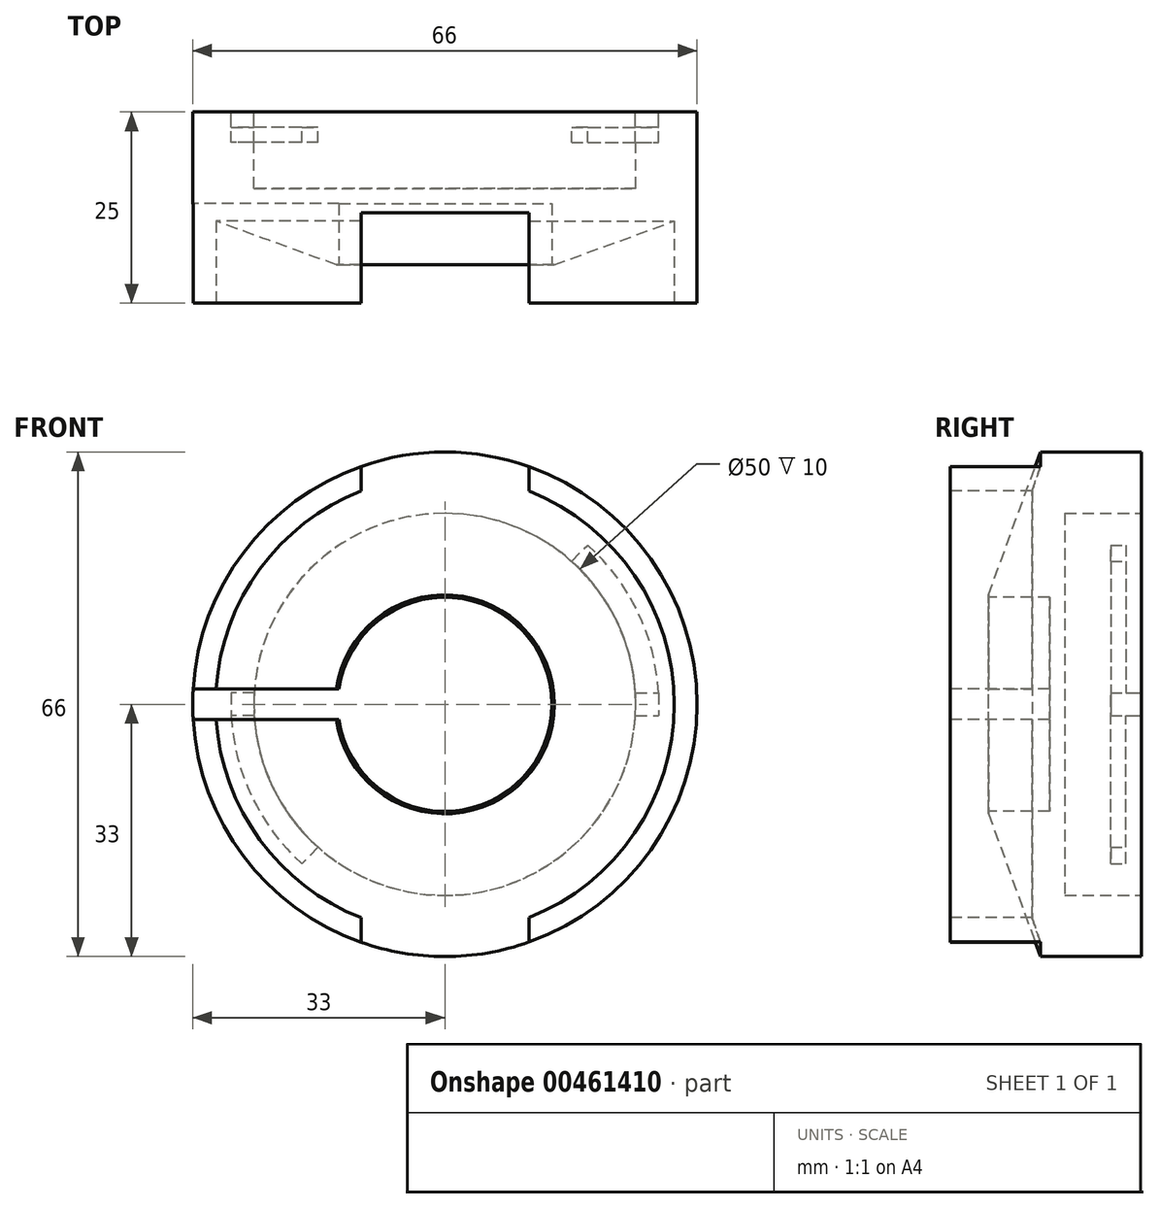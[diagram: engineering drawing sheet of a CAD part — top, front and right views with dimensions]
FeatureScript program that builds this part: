
annotation { "Feature Type Name" : "Feature", "Feature Type Description" : "" }
export const myFeature = defineFeature(function(context is Context, id is Id, definition is map)
    precondition{}
    {
        {
            var Q0;
            Q0=qCreatedBy(makeId("Front.planeOp"),FACE);
            var sketch = newSketch(context, id + "F0", { "sketchPlane" : qUnion([Q0])});
            skCircle(sketch, "E0", {"center": v(0, 0) * mm, "radius": 30 * mm});
            skSolve(sketch);
        }
        {
            var Q0;
            Q0 = qSketchRegion(id + "F0", true);
            extrude(context, id + "F1", {"entities" : qUnion([Q0]), "depth" : 20 * mm});
        }
        {
            var Q0;
            Q0=makeQuery(id+"F1.opExtrude","CAP_FACE",FACE,{"disambiguationData":[OSD([sQuery(id+"F0.wireOp",EDGE,"E0")])],"isStart":false});
            var sketch = newSketch(context, id + "F2", { "sketchPlane" : qUnion([Q0])});
            skCircle(sketch, "E1", {"center": v(0, 0) * mm, "radius": 33 * mm});
            skCircle(sketch, "E2", {"center": v(0, 0) * mm, "radius": 30 * mm});
            skSolve(sketch);
        }
        {
            var Q0;
            Q0=makeQuery(id+"F2.imprint","IMPRINT",FACE,{"disambiguationData":[TD([[makeQuery(id+"F2.imprint","IMPRINT",EDGE,{"derivedFrom":sQuery(id+"F2.wireOp",EDGE,"E1")}),1.0]])]});
            var Q1;
            Q1=makeQuery(id+"F1.opExtrude","CAP_FACE",FACE,{"disambiguationData":[OSD([sQuery(id+"F0.wireOp",EDGE,"E0")])],"isStart":true});
            extrude(context, id + "F3", {"entities" : qUnion([Q0]), "operationType" : NewBodyOperationType.ADD, "endBound" : BoundingType.UP_TO_SURFACE, "oppositeDirection" : true, "endBoundEntityFace" : qUnion([Q1]), "depth" : 25 * mm, "hasSecondDirection" : true, "secondDirectionOppositeDirection" : false, "secondDirectionDepth" : 5 * mm});
        }
        {
            var Q0;
            Q0=makeQuery(id+"F1.opExtrude","CAP_FACE",FACE,{"disambiguationData":[OSD([sQuery(id+"F0.wireOp",EDGE,"E0")])],"isStart":false});
            var sketch = newSketch(context, id + "F4", { "sketchPlane" : qUnion([Q0])});
            skCircle(sketch, "E3", {"center": v(0, 0) * mm, "radius": 14 * mm});
            skSolve(sketch);
        }
        {
            var Q0;
            Q0 = qSketchRegion(id + "F4", true);
            extrude(context, id + "F5", {"entities" : qUnion([Q0]), "operationType" : NewBodyOperationType.REMOVE, "oppositeDirection" : true, "depth" : 8 * mm});
        }
        {
            var Q0;
            Q0=makeQuery(id+"F3.opExtrude","CAP_FACE",FACE,{"disambiguationData":[OSD([sQuery(id+"F2.wireOp",EDGE,"E1"),sQuery(id+"F2.wireOp",EDGE,"E2")])],"isStart":true});
            var sketch = newSketch(context, id + "F6", { "sketchPlane" : qUnion([Q0])});
            skLineSegment(sketch, "E4.bottom", {"start": v(-33, 2) * mm, "end": v(0, 2) * mm});
            skLineSegment(sketch, "E4.top", {"start": v(-33, -2) * mm, "end": v(0, -2) * mm});
            skLineSegment(sketch, "E4.left", {"start": v(-33, 2) * mm, "end": v(-33, -2) * mm});
            skLineSegment(sketch, "E4.right", {"start": v(0, 2) * mm, "end": v(0, -2) * mm});
            skSolve(sketch);
        }
        {
            var Q0;
            Q0 = qSketchRegion(id + "F6", true);
            var Q1;
            Q1=makeQuery(id+"F5.boolean.opBoolean","COPY",FACE,{"derivedFrom":makeQuery(id+"F5.opExtrude","CAP_FACE",FACE,{"disambiguationData":[OSD([sQuery(id+"F4.wireOp",EDGE,"E3")])],"isStart":false})});
            extrude(context, id + "F7", {"entities" : qUnion([Q0]), "operationType" : NewBodyOperationType.REMOVE, "endBound" : BoundingType.UP_TO_SURFACE, "oppositeDirection" : true, "endBoundEntityFace" : qUnion([Q1]), "depth" : 25 * mm});
        }
        {
            var Q0;
            Q0=makeQuery(id+"F3.opExtrude","CAP_FACE",FACE,{"disambiguationData":[OSD([sQuery(id+"F2.wireOp",EDGE,"E1"),sQuery(id+"F2.wireOp",EDGE,"E2")])],"isStart":true});
            var sketch = newSketch(context, id + "F8", { "sketchPlane" : qUnion([Q0])});
            skLineSegment(sketch, "E5.bottom", {"start": v(-10.97, 33) * mm, "end": v(11.03, 33) * mm});
            skLineSegment(sketch, "E5.top", {"start": v(-10.97, -33) * mm, "end": v(11.03, -33) * mm});
            skLineSegment(sketch, "E5.left", {"start": v(-10.97, 33) * mm, "end": v(-10.97, -33) * mm});
            skLineSegment(sketch, "E5.right", {"start": v(11.03, 33) * mm, "end": v(11.03, -33) * mm});
            skLineSegment(sketch, "E6", {"start": v(33, 0) * mm, "end": v(33, 26.84) * mm, "construction": true});
            skLineSegment(sketch, "E7", {"start": v(33, 26.84) * mm, "end": v(33, -25.37) * mm, "construction": true});
            skLineSegment(sketch, "E8.MirrorCS", {"start": v(-33, 26.84) * mm, "end": v(-33, -25.37) * mm, "construction": true});
            skLineSegment(sketch, "E9", {"start": v(33, 0) * mm, "end": v(11.03, 0) * mm, "construction": true});
            skLineSegment(sketch, "E10", {"start": v(-10.97, 0) * mm, "end": v(-32.94, 0) * mm, "construction": true});
            skSolve(sketch);
        }
        {
            var Q0;
            Q0 = qSketchRegion(id + "F8", true);
            var Q1;
            Q1=makeQuery(id+"F1.opExtrude","CAP_FACE",FACE,{"disambiguationData":[OSD([sQuery(id+"F0.wireOp",EDGE,"E0")])],"isStart":false});
            extrude(context, id + "F9", {"entities" : qUnion([Q0]), "operationType" : NewBodyOperationType.REMOVE, "endBound" : BoundingType.UP_TO_SURFACE, "oppositeDirection" : true, "endBoundEntityFace" : qUnion([Q1]), "depth" : 25 * mm});
        }
        {
            var Q0;
            Q0=makeQuery(id+"F3.boolean.opBoolean","MERGE",FACE,{"derivedFrom":[makeQuery(id+"F1.opExtrude","CAP_FACE",FACE,{"disambiguationData":[OSD([sQuery(id+"F0.wireOp",EDGE,"E0")])],"isStart":true}),makeQuery(id+"F3.opExtrude","CAP_FACE",FACE,{"disambiguationData":[OSD([sQuery(id+"F2.wireOp",EDGE,"E1"),sQuery(id+"F2.wireOp",EDGE,"E2")])],"isStart":false})]});
            var sketch = newSketch(context, id + "F10", { "sketchPlane" : qUnion([Q0])});
            skCircle(sketch, "E11", {"center": v(0, 0) * mm, "radius": 25 * mm});
            skSolve(sketch);
        }
        {
            var Q0;
            Q0 = qSketchRegion(id + "F10", true);
            extrude(context, id + "F11", {"entities" : qUnion([Q0]), "operationType" : NewBodyOperationType.REMOVE, "oppositeDirection" : true, "depth" : 10 * mm});
        }
        {
            var Q0;
            Q0=makeQuery(id+"F3.boolean.opBoolean","MERGE",FACE,{"derivedFrom":[makeQuery(id+"F1.opExtrude","CAP_FACE",FACE,{"disambiguationData":[OSD([sQuery(id+"F0.wireOp",EDGE,"E0")])],"isStart":true}),makeQuery(id+"F3.opExtrude","CAP_FACE",FACE,{"disambiguationData":[OSD([sQuery(id+"F2.wireOp",EDGE,"E1"),sQuery(id+"F2.wireOp",EDGE,"E2")])],"isStart":false})]});
            var sketch = newSketch(context, id + "F12", { "sketchPlane" : qUnion([Q0])});
            skLineSegment(sketch, "E12.bottom", {"start": v(-24.95, 1.5) * mm, "end": v(-27.95, 1.5) * mm});
            skLineSegment(sketch, "E12.top", {"start": v(-24.95, -1.5) * mm, "end": v(-27.95, -1.5) * mm});
            skLineSegment(sketch, "E12.left", {"start": v(-24.95, 1.5) * mm, "end": v(-24.95, -1.5) * mm});
            skLineSegment(sketch, "E12.right", {"start": v(-27.95, 1.5) * mm, "end": v(-27.95, -1.5) * mm});
            skPoint(sketch, "E12.middle", {"position": v(-26.45, 0) * mm});
            skLineSegment(sketch, "E13.MirrorCS", {"start": v(24.95, 1.5) * mm, "end": v(27.95, 1.5) * mm});
            skLineSegment(sketch, "E14.MirrorCS", {"start": v(24.95, -1.5) * mm, "end": v(27.95, -1.5) * mm});
            skLineSegment(sketch, "E15.MirrorCS", {"start": v(24.95, 1.5) * mm, "end": v(24.95, -1.5) * mm});
            skLineSegment(sketch, "E16.MirrorCS", {"start": v(27.95, 1.5) * mm, "end": v(27.95, -1.5) * mm});
            skPoint(sketch, "E17.MirrorP", {"position": v(26.45, 0) * mm});
            skSolve(sketch);
        }
        {
            var Q0;
            Q0 = qSketchRegion(id + "F12", true);
            extrude(context, id + "F13", {"entities" : qUnion([Q0]), "operationType" : NewBodyOperationType.REMOVE, "oppositeDirection" : true, "depth" : 4 * mm});
        }
        {
            var Q0;
            Q0=makeQuery(id+"F13.boolean.opBoolean","COPY",FACE,{"derivedFrom":makeQuery(id+"F13.opExtrude","SWEPT_FACE",FACE,{"disambiguationData":[OSD([sQuery(id+"F12.wireOp",EDGE,"E14.MirrorCS")])]})});
            var sketch = newSketch(context, id + "F14", { "sketchPlane" : qUnion([Q0])});
            skLineSegment(sketch, "E18.bottom", {"start": v(-27.95, -4) * mm, "end": v(-24.95, -4) * mm});
            skLineSegment(sketch, "E18.top", {"start": v(-27.95, -2) * mm, "end": v(-24.95, -2) * mm});
            skLineSegment(sketch, "E18.left", {"start": v(-27.95, -4) * mm, "end": v(-27.95, -2) * mm});
            skLineSegment(sketch, "E18.right", {"start": v(-24.95, -4) * mm, "end": v(-24.95, -2) * mm});
            skSolve(sketch);
        }
        {
            var Q0;
            Q0 = qSketchRegion(id + "F14", true);
            var Q1;
            Q1=makeQuery(id+"F11.boolean.opBoolean","COPY",FACE,{"derivedFrom":makeQuery(id+"F11.opExtrude","SWEPT_FACE",FACE,{"disambiguationData":[OSD([sQuery(id+"F10.wireOp",EDGE,"E11")])]})});
            revolve(context, id + "F15", {"operationType" : NewBodyOperationType.REMOVE, "entities" : qUnion([Q0]), "axis" : qUnion([Q1]), "revolveType" : RevolveType.ONE_DIRECTION, "angle" : 45 * degree});
        }
        {
            var Q0;
            Q0=makeQuery(id+"F13.boolean.opBoolean","COPY",FACE,{"derivedFrom":makeQuery(id+"F13.opExtrude","SWEPT_FACE",FACE,{"disambiguationData":[OSD([sQuery(id+"F12.wireOp",EDGE,"E12.bottom")])]})});
            var sketch = newSketch(context, id + "F16", { "sketchPlane" : qUnion([Q0])});
            skLineSegment(sketch, "E19.bottom", {"start": v(27.95, 4) * mm, "end": v(24.95, 4) * mm});
            skLineSegment(sketch, "E19.top", {"start": v(27.95, 2) * mm, "end": v(24.95, 2) * mm});
            skLineSegment(sketch, "E19.left", {"start": v(27.95, 4) * mm, "end": v(27.95, 2) * mm});
            skLineSegment(sketch, "E19.right", {"start": v(24.95, 4) * mm, "end": v(24.95, 2) * mm});
            skSolve(sketch);
        }
        {
            var Q0;
            Q0 = qSketchRegion(id + "F16", true);
            var Q1;
            Q1=makeQuery(id+"F11.boolean.opBoolean","COPY",FACE,{"derivedFrom":makeQuery(id+"F11.opExtrude","SWEPT_FACE",FACE,{"disambiguationData":[OSD([sQuery(id+"F10.wireOp",EDGE,"E11")])]})});
            revolve(context, id + "F17", {"operationType" : NewBodyOperationType.REMOVE, "entities" : qUnion([Q0]), "axis" : qUnion([Q1]), "revolveType" : RevolveType.ONE_DIRECTION, "angle" : 45 * degree});
        }
        {
            var Q0;
            Q0=makeQuery(id+"F9.boolean.opBoolean","INTERSECT",EDGE,{"disambiguationData":[OD(0.0)],"derivedFrom":[makeQuery(id+"F3.opExtrude","SWEPT_FACE",FACE,{"disambiguationData":[OSD([sQuery(id+"F2.wireOp",EDGE,"E1")])]}),makeQuery(id+"F9.opExtrude","CAP_FACE",FACE,{"disambiguationData":[OSD([sQuery(id+"F8.wireOp",EDGE,"E5.bottom"),sQuery(id+"F8.wireOp",EDGE,"E5.top"),sQuery(id+"F8.wireOp",EDGE,"E5.left"),sQuery(id+"F8.wireOp",EDGE,"E5.right")])],"isStart":false})]});
            chamfer(context, id + "F18", {"entities" : qUnion([Q0]), "chamferType" : ChamferType.OFFSET_ANGLE, "width" : 6.8 * mm, "oppositeDirection" : false, "angle" : 70 * degree, "tangentPropagation" : true});
        }
    });
